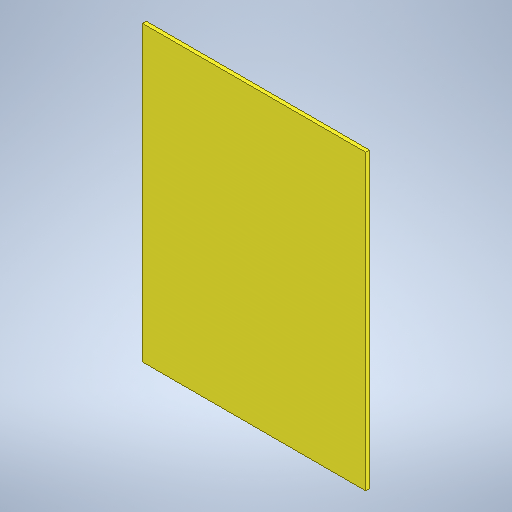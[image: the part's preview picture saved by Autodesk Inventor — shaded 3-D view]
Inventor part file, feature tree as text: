
AUTODESK INVENTOR PART (.ipt)
format: ipt  version: 2025 (Build 290162010, 162A)  size: 245,248 bytes
history: native  units: in
note: dims shown in document units (in); Inventor stores cm internally (conversion verified against a paired STEP export)
features: extrude x1, sketch x1
ambient origin geometry x8: Origin, YZ Plane, XZ Plane, XY Plane, X Axis, Y Axis, Z Axis, Center Point
bodies: Solid1 (feature_tree)
feature tree (2):
  extrude  "Extrusion1"  Depth=36.5in
  sketch  "Sketch1"  dims[d2=48.0in d3=36.5in d4=0.625in d5=0.0in]
